# Revit family: KOROBKA SOEDINITELNAYa KVSK «SEVER»
name_source: partatom
category: Датчики
units: mm (PartAtom-declared; Revit-internal decimal feet)

## family parameters
Всегда вертикально = Да
Заголовок OmniClass = Communication and Data Processing Equipment
На основе рабочей плоскости = Нет
Номер OmniClass = 23.85.50.17
Общий = Нет
При загрузке вырезать с полостями = Нет
Размер круглого соединителя = Использовать диаметр
Сохранять ориентацию аннотаций = Нет
Тип детали = Нормальный
Точка принадлежности помещению = Нет

## types (1)
- Коробка соединительная КВСК "СЕВЕР"
    ADSK_Единица измерения = шт.
    ADSK_Завод-изготовитель = ООО НПП «МАГНИТО-КОНТАКТ»
    ADSK_Масса = 1.2
    ADSK_Материал = Пластик белый
    ADSK_Наименование = Коробка соединительная КВСК "СЕВЕР"
    ADSK_Наименование краткое = КВСК
    ADSK_Обозначение = ПАШК.685552.002 ТУ
    ADSK_Примечание = Коробка имеет защиту от вскрытия с выводом контактов датчика на отдельный клеммник.
    ADSK_Размер_Высота = 93 мм
    ADSK_Размер_Длина = 302 мм
    ADSK_Размер_Ширина = 197 мм
    URL = https://m-kontakt.ru
    Диапазон рабочих температур = от -65 до +70
    Изготовитель = ООО НПП «МАГНИТО-КОНТАКТ»
    Кабельные вводы = Да
    Описание = Коробка соединительная предназначена для соединения (разветвления) сигнальных кабелей, например в шлейфах пожарной или охранно-пожарной сигнализации, линиях связи и телекоммуникаций, цепях систем управления и автоматики, а также подключения в шлейфы оконечных устройств и т. п.
    Отметка по умолчанию = 0 мм
    Переходное сопротивление двух контактов = не более 0,3
    Присоединительные размеры (длина) = 220 мм
    Присоединительные размеры (ширина) = 168 мм
    Срок службы = не менее 10 лет
    Степень защиты оболочки = IP66/IP67
